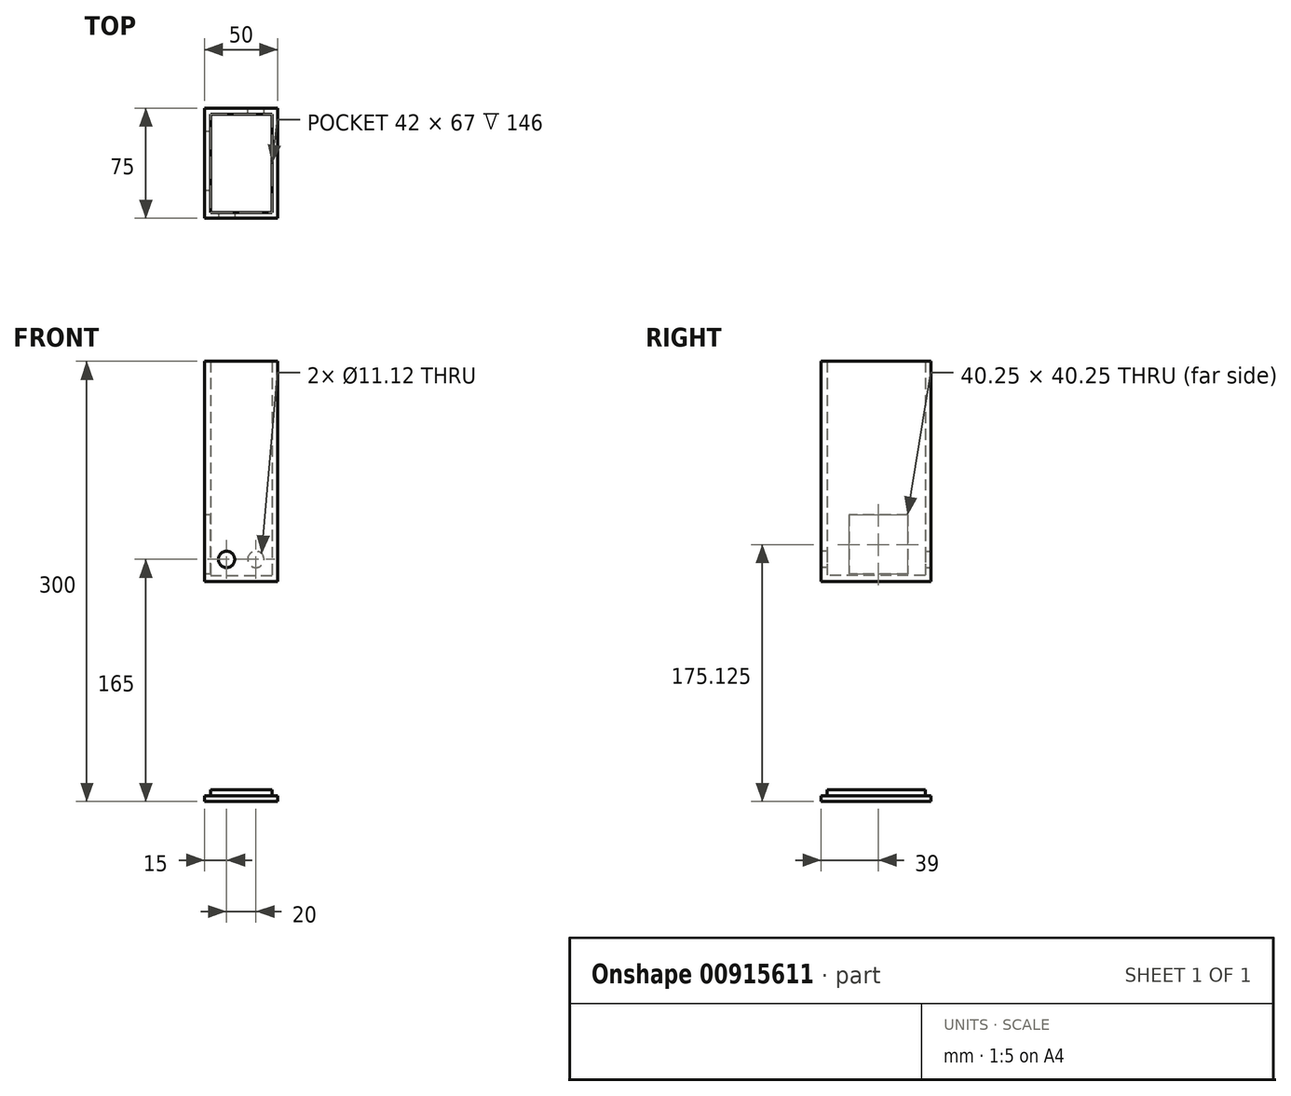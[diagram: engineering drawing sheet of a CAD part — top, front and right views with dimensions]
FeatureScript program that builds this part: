
annotation { "Feature Type Name" : "Feature", "Feature Type Description" : "" }
export const myFeature = defineFeature(function(context is Context, id is Id, definition is map)
    precondition{}
    {
        {
            var Q0;
            Q0=qCreatedBy(makeId("Top.planeOp"),FACE);
            var sketch = newSketch(context, id + "F0", { "sketchPlane" : qUnion([Q0])});
            skLineSegment(sketch, "E0", {"start": v(0, 0) * mm, "end": v(0, 36) * mm});
            skLineSegment(sketch, "E1", {"start": v(0, 36) * mm, "end": v(0, -39) * mm});
            skLineSegment(sketch, "E2", {"start": v(4, 32) * mm, "end": v(4, -35) * mm});
            skLineSegment(sketch, "E3.bottom", {"start": v(4, 32) * mm, "end": v(46, 32) * mm});
            skLineSegment(sketch, "E3.top", {"start": v(4, -35) * mm, "end": v(46, -35) * mm});
            skLineSegment(sketch, "E3.right", {"start": v(46, 32) * mm, "end": v(46, -35) * mm});
            skLineSegment(sketch, "E4.right", {"start": v(50, 36) * mm, "end": v(50, -39) * mm});
            skLineSegment(sketch, "E5", {"start": v(0, -39) * mm, "end": v(50, -39) * mm});
            skLineSegment(sketch, "E6", {"start": v(0, 36) * mm, "end": v(50, 36) * mm});
            skSolve(sketch);
        }
        {
            var Q0;
            {var subQ0=sQuery(id+"F0.wireOp",EDGE,"xSKNRjzc-Q0CY-HxQO-JAmt-7Oy3DvpnzF8y");Q0=makeQuery(id+"F0.imprint","IMPRINT",FACE,{"disambiguationData":[TD([[makeQuery(id+"F0.imprint","IMPRINT",EDGE,{"derivedFrom":subQ0}),1.0]])]});}
            var Q1;
            Q1=makeQuery(id+"F0.imprint","IMPRINT",FACE,{"disambiguationData":[TD([[makeQuery(id+"F0.imprint","IMPRINT",EDGE,{"derivedFrom":sQuery(id+"F0.wireOp",EDGE,"E3.bottom")}),1.0]])]});
            extrude(context, id + "F1", {"entities" : qUnion([Q0, Q1]), "depth" : 150 * mm, "offsetDistance" : 25 * mm});
        }
        {
            var Q0;
            Q0=makeQuery(id+"F0.imprint","IMPRINT",FACE,{"disambiguationData":[TD([[makeQuery(id+"F0.imprint","IMPRINT",EDGE,{"derivedFrom":sQuery(id+"F0.wireOp",EDGE,"E3.bottom")}),-1.0]])]});
            extrude(context, id + "F2", {"entities" : qUnion([Q0]), "operationType" : NewBodyOperationType.ADD, "depth" : 4 * mm, "offsetDistance" : 25 * mm});
        }
        {
            var Q0;
            Q0=makeQuery(id+"F2.opExtrude","CAP_FACE",FACE,{"disambiguationData":[OSD([sQuery(id+"F0.wireOp",EDGE,"RdLhT0QT-N1Sc-ESqN-lxrp-yrU2ipRMtyYH"),sQuery(id+"F0.wireOp",EDGE,"E2")])],"isStart":false});
            var Q1;
            {var subQ0=sQuery(id+"F0.wireOp",EDGE,"E3.right");var subQ1=sQuery(id+"F0.wireOp",EDGE,"E2");var subQ2=sQuery(id+"F0.wireOp",EDGE,"E3.top");var subQ3=sQuery(id+"F0.wireOp",EDGE,"E3.bottom");Q1=makeQuery(id+"F2.boolean.opBoolean","MERGE",FACE,{"derivedFrom":[makeQuery(id+"F1.opExtrude","CAP_FACE",FACE,{"disambiguationData":[OSD([subQ3,subQ2,subQ1,subQ0,sQuery(id+"F0.wireOp",EDGE,"E1"),sQuery(id+"F0.wireOp",EDGE,"E4.right"),sQuery(id+"F0.wireOp",EDGE,"E5"),sQuery(id+"F0.wireOp",EDGE,"E6")])],"isStart":true}),makeQuery(id+"F2.opExtrude","CAP_FACE",FACE,{"disambiguationData":[OSD([subQ3,subQ2,subQ1,subQ0])],"isStart":true})]});}
            extrude(context, id + "F3", {"entities" : qUnion([Q0, Q1]), "operationType" : NewBodyOperationType.ADD, "oppositeDirection" : true, "depth" : 150 * mm, "offsetDistance" : 25 * mm, "hasSecondDirection" : true, "secondDirectionOppositeDirection" : false, "secondDirectionDepth" : -146 * mm});
        }
        {
            var Q0;
            Q0=makeQuery(id+"F1.opExtrude","SWEPT_FACE",FACE,{"disambiguationData":[OSD([sQuery(id+"F0.wireOp",EDGE,"E1")])]});
            var sketch = newSketch(context, id + "F4", { "sketchPlane" : qUnion([Q0])});
            skLineSegment(sketch, "E7.bottom", {"start": v(-20.12, 45.25) * mm, "end": v(20.12, 45.25) * mm});
            skLineSegment(sketch, "E7.top", {"start": v(-20.12, 5) * mm, "end": v(20.12, 5) * mm});
            skLineSegment(sketch, "E7.left", {"start": v(-20.12, 45.25) * mm, "end": v(-20.12, 5) * mm});
            skLineSegment(sketch, "E7.right", {"start": v(20.12, 45.25) * mm, "end": v(20.12, 5) * mm});
            skSolve(sketch);
        }
        {
            var Q0;
            Q0=makeQuery(id+"F4.imprint","IMPRINT",FACE,{"disambiguationData":[TD([[makeQuery(id+"F4.imprint","IMPRINT",EDGE,{"derivedFrom":sQuery(id+"F4.wireOp",EDGE,"E7.bottom")}),-1.0]])]});
            extrude(context, id + "F5", {"entities" : qUnion([Q0]), "operationType" : NewBodyOperationType.REMOVE, "oppositeDirection" : true, "depth" : 25 * mm, "offsetDistance" : 25 * mm});
        }
        {
            var Q0;
            Q0=makeQuery(id+"F1.opExtrude","SWEPT_FACE",FACE,{"disambiguationData":[OSD([sQuery(id+"F0.wireOp",EDGE,"E5")])]});
            var sketch = newSketch(context, id + "F6", { "sketchPlane" : qUnion([Q0])});
            skCircle(sketch, "E8", {"center": v(15, 15) * mm, "radius": 5.56 * mm});
            skSolve(sketch);
        }
        {
            var Q0;
            Q0=makeQuery(id+"F1.opExtrude","SWEPT_FACE",FACE,{"disambiguationData":[OSD([sQuery(id+"F0.wireOp",EDGE,"E6")])]});
            var sketch = newSketch(context, id + "F7", { "sketchPlane" : qUnion([Q0])});
            skCircle(sketch, "E9", {"center": v(-35, 15) * mm, "radius": 5.56 * mm});
            skSolve(sketch);
        }
        {
            var Q0;
            Q0=makeQuery(id+"F7.imprint","IMPRINT",FACE,{"disambiguationData":[TD([[makeQuery(id+"F7.imprint","IMPRINT",EDGE,{"derivedFrom":sQuery(id+"F7.wireOp",EDGE,"E9")}),1.0]])]});
            extrude(context, id + "F8", {"entities" : qUnion([Q0]), "operationType" : NewBodyOperationType.REMOVE, "oppositeDirection" : true, "depth" : 25 * mm, "offsetDistance" : 25 * mm});
        }
        {
            var Q0;
            Q0=makeQuery(id+"F6.imprint","IMPRINT",FACE,{"disambiguationData":[TD([[makeQuery(id+"F6.imprint","IMPRINT",EDGE,{"derivedFrom":sQuery(id+"F6.wireOp",EDGE,"E8")}),1.0]])]});
            var Q1;
            Q1=sQuery(id+"F6.wireOp",EDGE,"E8");
            extrude(context, id + "F9", {"entities" : qUnion([Q0]), "operationType" : NewBodyOperationType.REMOVE, "surfaceEntities" : qUnion([Q1]), "oppositeDirection" : true, "depth" : 25 * mm, "offsetDistance" : 25 * mm});
        }
        {
            var Q0;
            {var subQ0=sQuery(id+"F0.wireOp",EDGE,"E6");var subQ1=sQuery(id+"F0.wireOp",EDGE,"E5");var subQ2=sQuery(id+"F0.wireOp",EDGE,"E4.right");var subQ3=sQuery(id+"F0.wireOp",EDGE,"E1");var subQ4=sQuery(id+"F0.wireOp",EDGE,"E3.right");var subQ5=sQuery(id+"F0.wireOp",EDGE,"E2");var subQ6=sQuery(id+"F0.wireOp",EDGE,"E3.top");var subQ7=sQuery(id+"F0.wireOp",EDGE,"E3.bottom");Q0=makeQuery(id+"F3.boolean.opBoolean","MERGE",FACE,{"derivedFrom":[makeQuery(id+"F1.opExtrude","CAP_FACE",FACE,{"disambiguationData":[OSD([subQ7,subQ6,subQ5,subQ4,subQ3,subQ2,subQ1,subQ0])],"isStart":false}),makeQuery(id+"F3.opExtrude","CAP_FACE",FACE,{"disambiguationData":[OSD([subQ7,subQ6,subQ5,subQ4,subQ3,subQ2,subQ1,subQ0])],"isStart":false})]});}
            var sketch = newSketch(context, id + "F10", { "sketchPlane" : qUnion([Q0])});
            skCircle(sketch, "E10", {"center": v(29.88, 0) * mm, "radius": 5 * mm});
            skSolve(sketch);
        }
        {
            var Q0;
            Q0=makeQuery(id+"F10.imprint","IMPRINT",FACE,{"disambiguationData":[TD([[makeQuery(id+"F10.imprint","IMPRINT",EDGE,{"derivedFrom":sQuery(id+"F10.wireOp",EDGE,"E10")}),1.0]])]});
            extrude(context, id + "F11", {"entities" : qUnion([Q0]), "operationType" : NewBodyOperationType.REMOVE, "oppositeDirection" : true, "depth" : 25 * mm, "offsetDistance" : 25 * mm});
        }
    });
